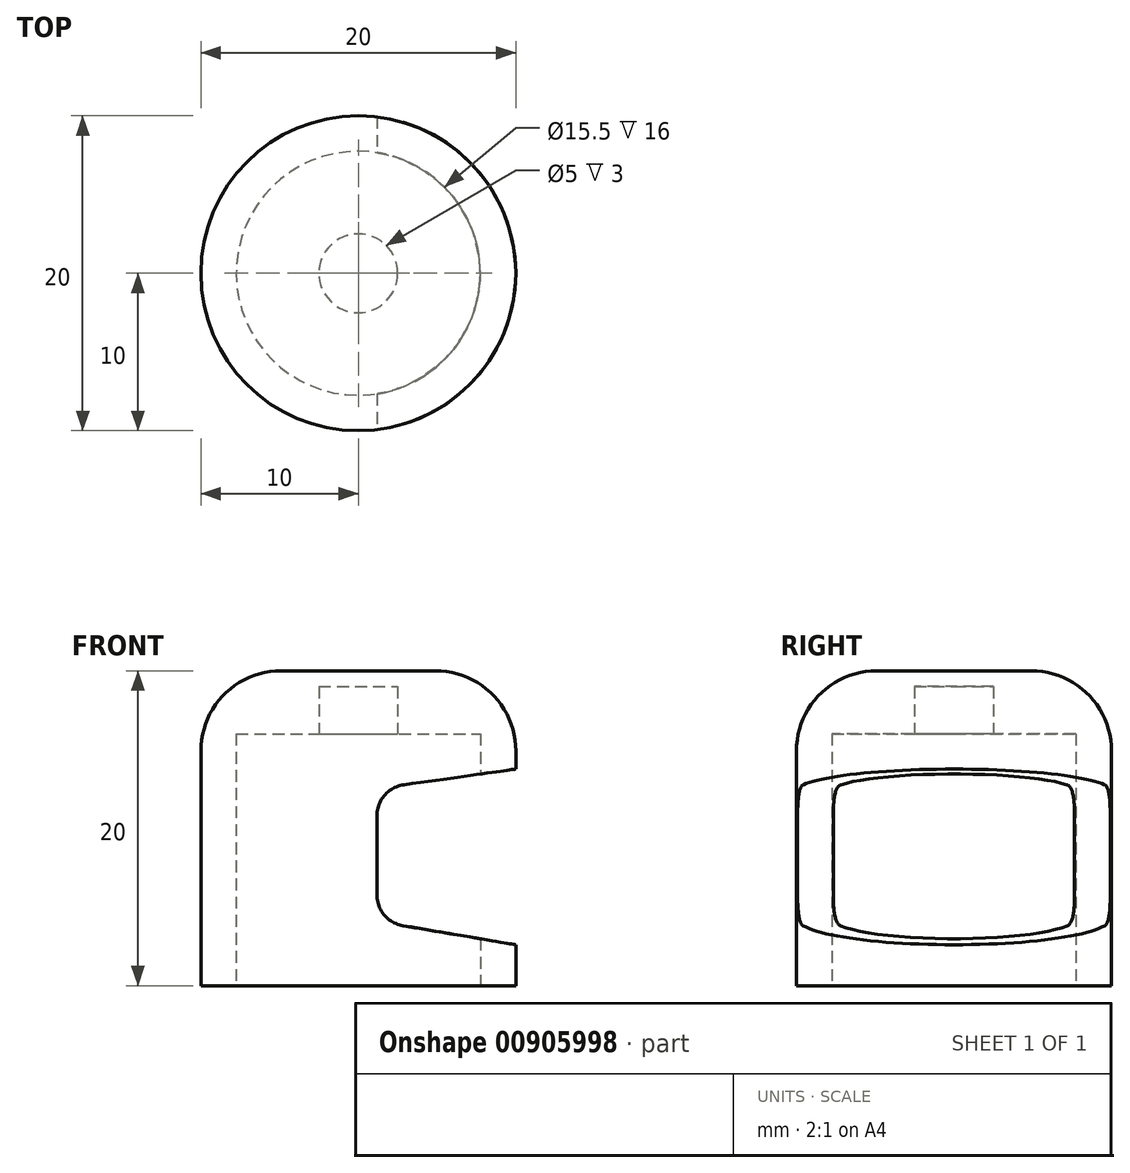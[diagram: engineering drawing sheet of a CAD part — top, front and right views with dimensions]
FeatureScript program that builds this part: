
annotation { "Feature Type Name" : "Feature", "Feature Type Description" : "" }
export const myFeature = defineFeature(function(context is Context, id is Id, definition is map)
    precondition{}
    {
        {
            var Q0;
            Q0=qCreatedBy(makeId("Top.planeOp"),FACE);
            var sketch = newSketch(context, id + "F0", { "sketchPlane" : qUnion([Q0])});
            skCircle(sketch, "E0", {"center": v(0, 0) * mm, "radius": 10 * mm});
            skSolve(sketch);
        }
        {
            var Q0;
            Q0=makeQuery(id+"F0.imprint","IMPRINT",FACE,{"disambiguationData":[TD([[makeQuery(id+"F0.imprint","IMPRINT",EDGE,{"derivedFrom":sQuery(id+"F0.wireOp",EDGE,"E0")}),1.0]])]});
            extrude(context, id + "F1", {"entities" : qUnion([Q0]), "depth" : 20 * mm, "offsetDistance" : 25.4 * mm});
        }
        {
            var Q0;
            Q0=qCreatedBy(makeId("Front.planeOp"),FACE);
            var sketch = newSketch(context, id + "F2", { "sketchPlane" : qUnion([Q0])});
            skLineSegment(sketch, "E1", {"start": v(10.82, 13.87) * mm, "end": v(2.9, 12.76) * mm});
            skLineSegment(sketch, "E2", {"start": v(1.18, 10.78) * mm, "end": v(1.18, 5.78) * mm});
            skLineSegment(sketch, "E3", {"start": v(2.84, 3.8) * mm, "end": v(13.2, 2.05) * mm});
            skPoint(sketch, "E4.visualSharp", {"position": v(1.18, 12.52) * mm});
            skArc(sketch, "E4.filletArc", {"start": v(2.9, 12.76) * mm, "mid": v(1.67, 12.1) * mm, "end": v(1.18, 10.78) * mm});
            skPoint(sketch, "E5.visualSharp", {"position": v(1.18, 4.1) * mm});
            skArc(sketch, "E5.filletArc", {"start": v(1.18, 5.78) * mm, "mid": v(1.65, 4.49) * mm, "end": v(2.84, 3.8) * mm});
            skLineSegment(sketch, "E6", {"start": v(10.82, 13.87) * mm, "end": v(13.2, 2.05) * mm});
            skSolve(sketch);
        }
        {
            var Q0;
            Q0=makeQuery(id+"F1.opExtrude","CAP_EDGE",EDGE,{"disambiguationData":[OSD([sQuery(id+"F0.wireOp",EDGE,"E0")])],"isStart":false});
            fillet(context, id + "F3", {"entities" : qUnion([Q0]), "radius" : 5.08 * mm, "tangentPropagation" : true, "allowEdgeOverflow" : false});
        }
        {
            var Q0;
            Q0 = qSketchRegion(id + "F2", true);
            extrude(context, id + "F4", {"entities" : qUnion([Q0]), "operationType" : NewBodyOperationType.REMOVE, "oppositeDirection" : true, "depth" : 25 * mm, "offsetDistance" : 25.4 * mm});
        }
        {
            var Q0;
            Q0=makeQuery(id+"F4.boolean.opBoolean","COPY",FACE,{"derivedFrom":makeQuery(id+"F4.opExtrude","CAP_FACE",FACE,{"disambiguationData":[OSD([sQuery(id+"F2.wireOp",EDGE,"E1"),sQuery(id+"F2.wireOp",EDGE,"E2"),sQuery(id+"F2.wireOp",EDGE,"E3"),sQuery(id+"F2.wireOp",EDGE,"E4.filletArc"),sQuery(id+"F2.wireOp",EDGE,"E5.filletArc"),sQuery(id+"F2.wireOp",EDGE,"E6")])],"isStart":true})});
            extrude(context, id + "F5", {"entities" : qUnion([Q0]), "operationType" : NewBodyOperationType.REMOVE, "oppositeDirection" : true, "depth" : 25.4 * mm, "offsetDistance" : 25.4 * mm});
        }
        {
            var Q0;
            Q0=makeQuery(id+"F1.opExtrude","CAP_FACE",FACE,{"disambiguationData":[OSD([sQuery(id+"F0.wireOp",EDGE,"E0")])],"isStart":true});
            var sketch = newSketch(context, id + "F6", { "sketchPlane" : qUnion([Q0])});
            skCircle(sketch, "E7", {"center": v(0, 0) * mm, "radius": 7.75 * mm});
            skSolve(sketch);
        }
        {
            var Q0;
            Q0=makeQuery(id+"F6.imprint","IMPRINT",FACE,{"disambiguationData":[TD([[makeQuery(id+"F6.imprint","IMPRINT",EDGE,{"derivedFrom":sQuery(id+"F6.wireOp",EDGE,"E7")}),1.0]])]});
            extrude(context, id + "F7", {"entities" : qUnion([Q0]), "operationType" : NewBodyOperationType.REMOVE, "oppositeDirection" : true, "depth" : 16 * mm, "offsetDistance" : 25.4 * mm});
        }
        {
            var Q0;
            Q0=makeQuery(id+"F7.boolean.opBoolean","COPY",FACE,{"derivedFrom":makeQuery(id+"F7.opExtrude","CAP_FACE",FACE,{"disambiguationData":[OSD([sQuery(id+"F6.wireOp",EDGE,"E7")])],"isStart":false})});
            var sketch = newSketch(context, id + "F8", { "sketchPlane" : qUnion([Q0])});
            skCircle(sketch, "E8", {"center": v(0, 0) * mm, "radius": 2.5 * mm});
            skSolve(sketch);
        }
        {
            var Q0;
            Q0=makeQuery(id+"F8.imprint","IMPRINT",FACE,{"disambiguationData":[TD([[makeQuery(id+"F8.imprint","IMPRINT",EDGE,{"derivedFrom":sQuery(id+"F8.wireOp",EDGE,"E8")}),1.0]])]});
            extrude(context, id + "F9", {"entities" : qUnion([Q0]), "operationType" : NewBodyOperationType.REMOVE, "oppositeDirection" : true, "depth" : 3 * mm, "offsetDistance" : 25.4 * mm});
        }
    });
